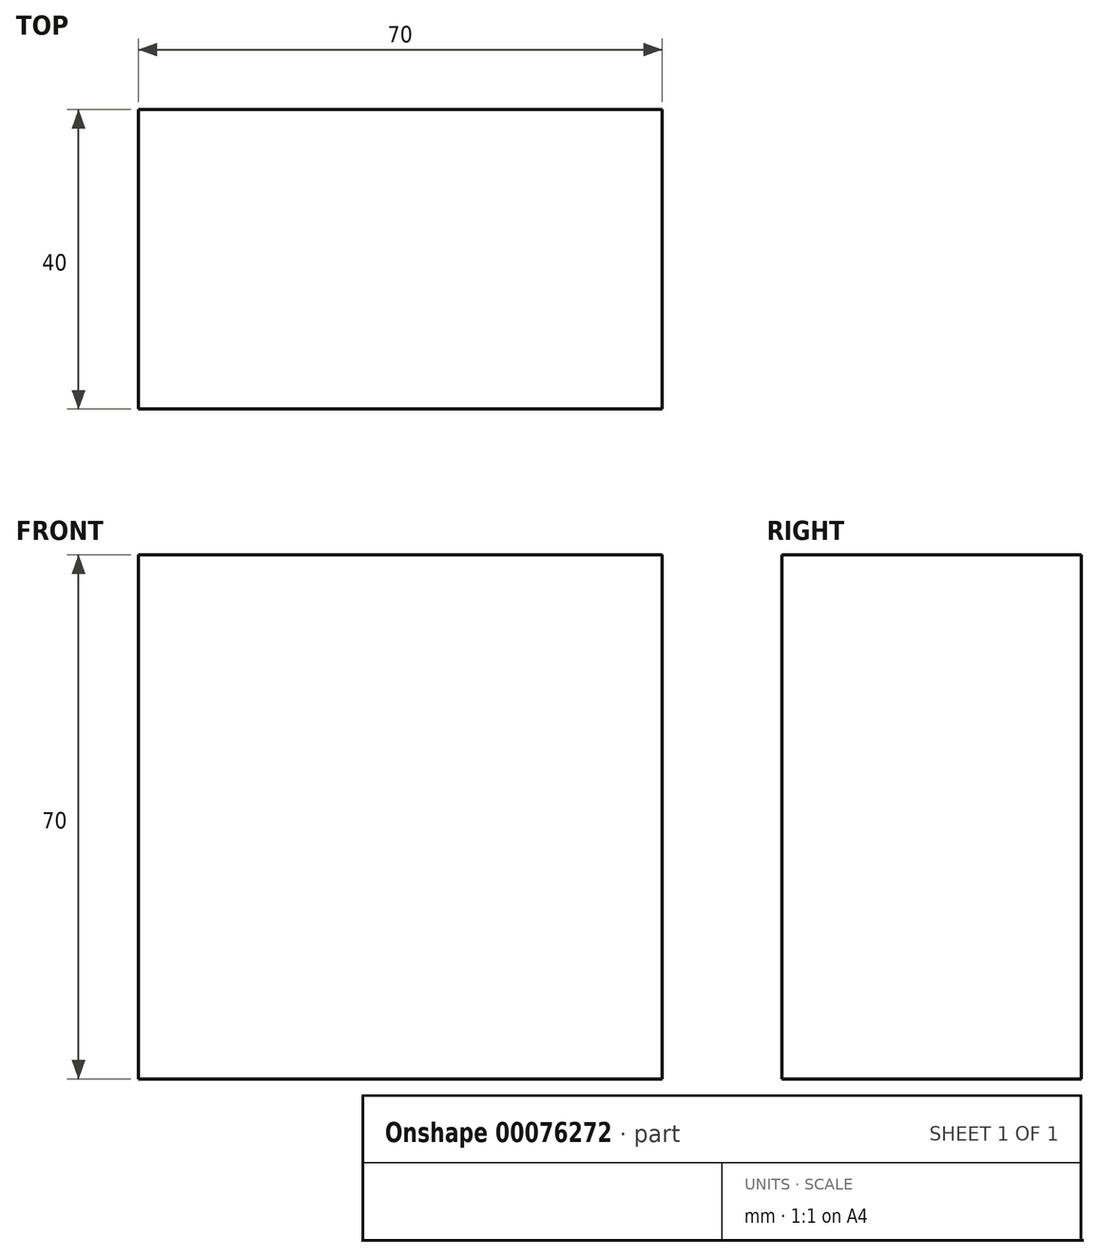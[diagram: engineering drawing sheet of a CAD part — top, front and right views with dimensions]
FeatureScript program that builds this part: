
annotation { "Feature Type Name" : "Feature", "Feature Type Description" : "" }
export const myFeature = defineFeature(function(context is Context, id is Id, definition is map)
    precondition{}
    {
        {
            var Q0;
            Q0=qCreatedBy(makeId("Front.planeOp"),FACE);
            var sketch = newSketch(context, id + "F0", { "sketchPlane" : qUnion([Q0])});
            skLineSegment(sketch, "E0.bottom", {"start": v(0, 0) * mm, "end": v(-70, 0) * mm});
            skLineSegment(sketch, "E0.top", {"start": v(0, 70) * mm, "end": v(-70, 70) * mm});
            skLineSegment(sketch, "E0.left", {"start": v(0, 0) * mm, "end": v(0, 70) * mm});
            skLineSegment(sketch, "E0.right", {"start": v(-70, 0) * mm, "end": v(-70, 70) * mm});
            skSolve(sketch);
        }
        {
            var Q0;
            Q0 = qSketchRegion(id + "F0", true);
            extrude(context, id + "F1", {"entities" : qUnion([Q0]), "depth" : 40 * mm});
        }
    });
